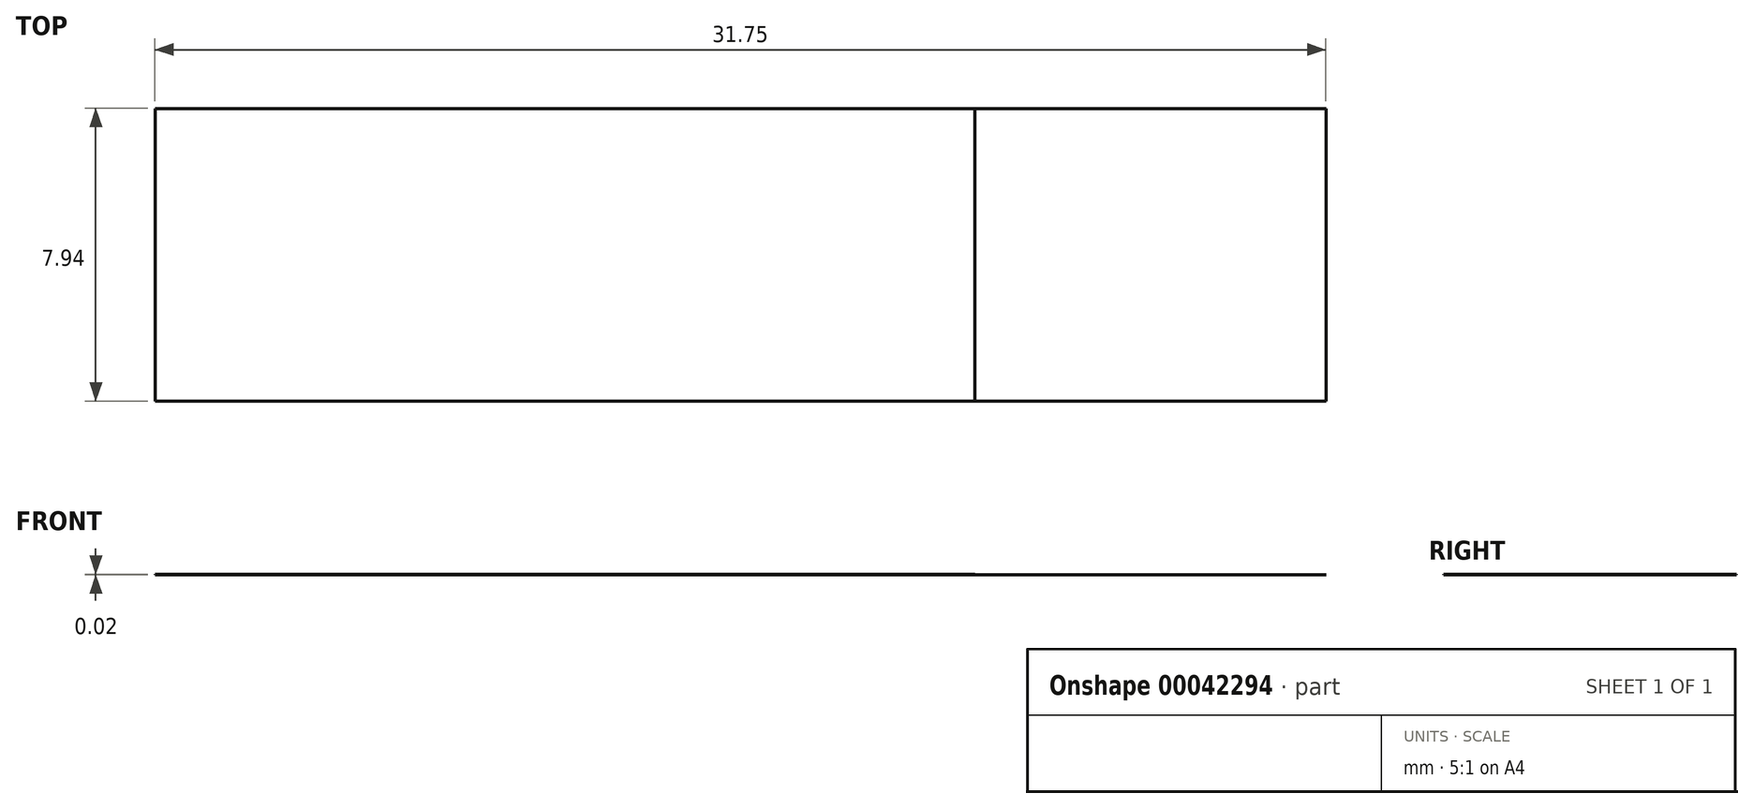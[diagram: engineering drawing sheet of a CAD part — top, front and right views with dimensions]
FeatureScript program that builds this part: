
annotation { "Feature Type Name" : "Feature", "Feature Type Description" : "" }
export const myFeature = defineFeature(function(context is Context, id is Id, definition is map)
    precondition{}
    {
        {
            var Q0;
            Q0=qCreatedBy(makeId("Top.planeOp"),FACE);
            var sketch = newSketch(context, id + "F0", { "sketchPlane" : qUnion([Q0])});
            skLineSegment(sketch, "E0", {"start": v(-15.96, 16.68) * mm, "end": v(15.8, 16.68) * mm});
            skLineSegment(sketch, "E1", {"start": v(15.8, 16.68) * mm, "end": v(15.8, 8.74) * mm});
            skLineSegment(sketch, "E2", {"start": v(15.8, 8.74) * mm, "end": v(-15.96, 8.74) * mm});
            skLineSegment(sketch, "E3", {"start": v(-15.96, 8.74) * mm, "end": v(-15.96, 16.68) * mm});
            skSolve(sketch);
        }
        {
            var Q0;
            Q0 = qSketchRegion(id + "F0", true);
            extrude(context, id + "F1", {"entities" : qUnion([Q0]), "depth" : 7 / 406.4 * mm});
        }
        {
            var Q0;
            Q0=makeQuery(id+"F1.opExtrude","CAP_FACE",FACE,{"disambiguationData":[OSD([sQuery(id+"F0.wireOp",EDGE,"E0"),sQuery(id+"F0.wireOp",EDGE,"E1"),sQuery(id+"F0.wireOp",EDGE,"E2"),sQuery(id+"F0.wireOp",EDGE,"E3")])],"isStart":false});
            var sketch = newSketch(context, id + "F2", { "sketchPlane" : qUnion([Q0])});
            skLineSegment(sketch, "E4", {"start": v(15.8, 16.68) * mm, "end": v(6.27, 16.68) * mm});
            skLineSegment(sketch, "E5", {"start": v(6.27, 16.68) * mm, "end": v(6.27, 8.74) * mm});
            skLineSegment(sketch, "E6", {"start": v(6.27, 8.74) * mm, "end": v(15.8, 8.74) * mm});
            skLineSegment(sketch, "E7", {"start": v(15.8, 8.74) * mm, "end": v(15.8, 16.68) * mm});
            skSolve(sketch);
        }
        {
            var Q0;
            Q0 = qSketchRegion(id + "F2", true);
            extrude(context, id + "F3", {"entities" : qUnion([Q0]), "operationType" : NewBodyOperationType.REMOVE, "oppositeDirection" : true, "depth" : 6 / 406.4 * mm});
        }
        {
            var Q0;
            Q0=makeQuery(id+"F3.boolean.opBoolean","COPY",FACE,{"derivedFrom":makeQuery(id+"F3.opExtrude","SWEPT_FACE",FACE,{"disambiguationData":[OSD([sQuery(id+"F2.wireOp",EDGE,"E5")])]})});
            var sketch = newSketch(context, id + "F4", { "sketchPlane" : qUnion([Q0])});
            skLineSegment(sketch, "E8", {"start": v(15.09, 1.59) * mm, "end": v(10.33, 1.59) * mm});
            skLineSegment(sketch, "E9", {"start": v(10.33, 1.59) * mm, "end": v(10.33, 11.11) * mm});
            skLineSegment(sketch, "E10", {"start": v(15.09, 1.59) * mm, "end": v(15.09, 11.11) * mm});
            skLineSegment(sketch, "E11", {"start": v(15.09, 11.11) * mm, "end": v(10.33, 11.11) * mm});
            skSolve(sketch);
        }
        {
            var Q0;
            Q0 = qSketchRegion(id + "F4", true);
            extrude(context, id + "F5", {"entities" : qUnion([Q0]), "operationType" : NewBodyOperationType.REMOVE, "endBound" : BoundingType.THROUGH_ALL, "oppositeDirection" : true, "depth" : 25.4 * mm});
        }
    });
